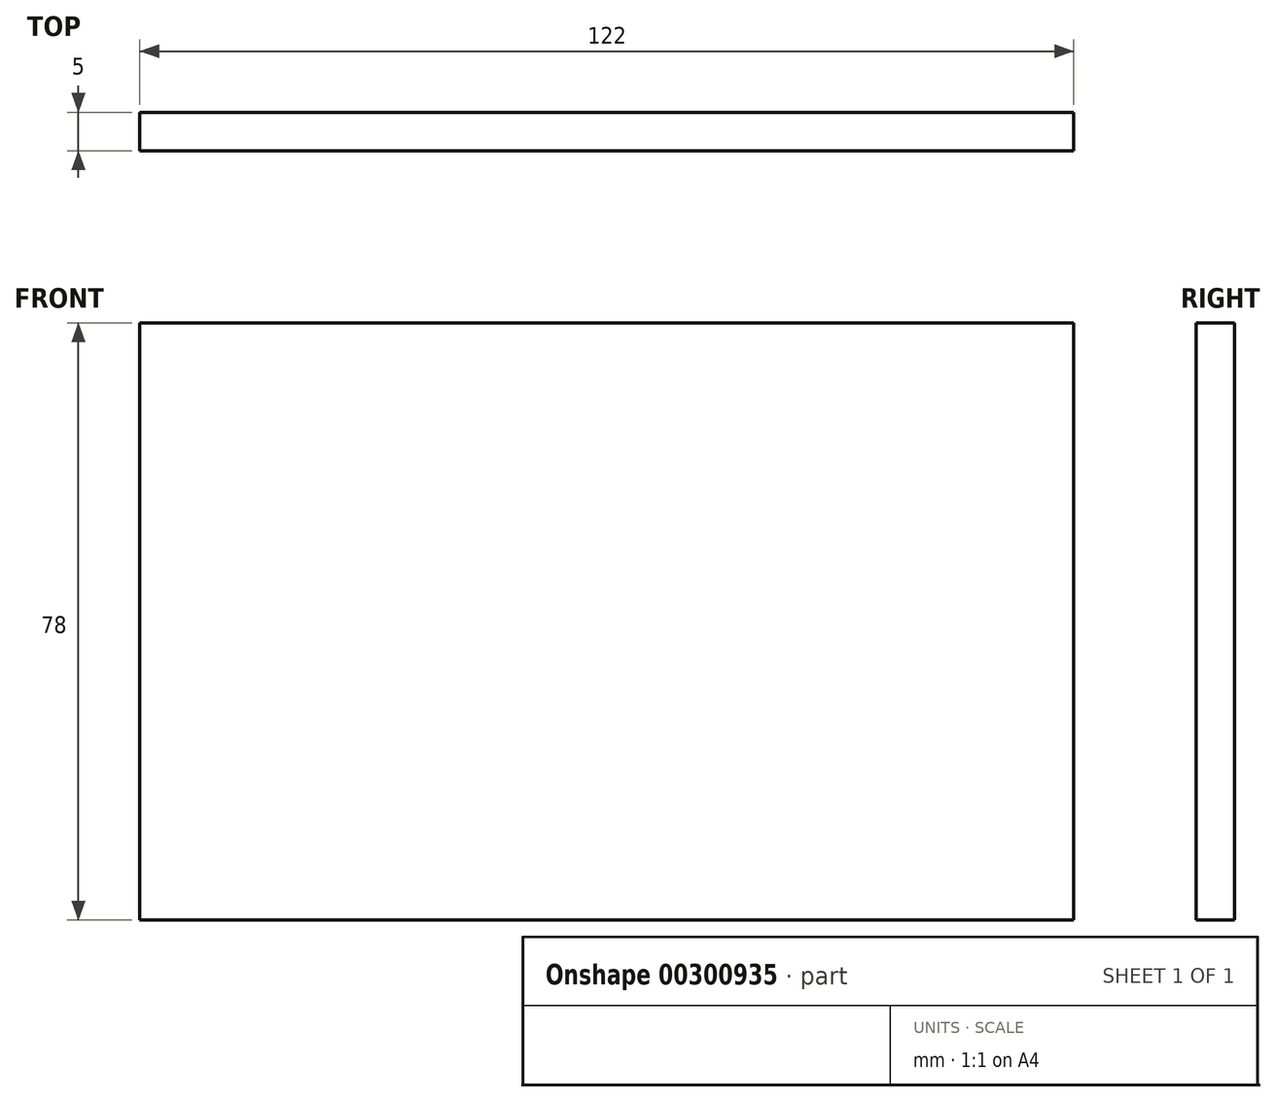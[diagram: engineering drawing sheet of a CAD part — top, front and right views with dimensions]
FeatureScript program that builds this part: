
annotation { "Feature Type Name" : "Feature", "Feature Type Description" : "" }
export const myFeature = defineFeature(function(context is Context, id is Id, definition is map)
    precondition{}
    {
        {
            var Q0;
            Q0=qCreatedBy(makeId("Front.planeOp"),FACE);
            var sketch = newSketch(context, id + "F0", { "sketchPlane" : qUnion([Q0])});
            skLineSegment(sketch, "E0.bottom", {"start": v(0, 0) * mm, "end": v(122, 0) * mm});
            skLineSegment(sketch, "E0.top", {"start": v(0, -78) * mm, "end": v(122, -78) * mm});
            skLineSegment(sketch, "E0.left", {"start": v(0, 0) * mm, "end": v(0, -78) * mm});
            skLineSegment(sketch, "E0.right", {"start": v(122, 0) * mm, "end": v(122, -78) * mm});
            skSolve(sketch);
        }
        {
            var Q0;
            Q0=makeQuery(id+"F0.imprint","IMPRINT",FACE,{"disambiguationData":[TD([[makeQuery(id+"F0.imprint","IMPRINT",EDGE,{"derivedFrom":sQuery(id+"F0.wireOp",EDGE,"E0.bottom")}),-1.0]])]});
            extrude(context, id + "F1", {"entities" : qUnion([Q0]), "depth" : 5 * mm});
        }
    });
